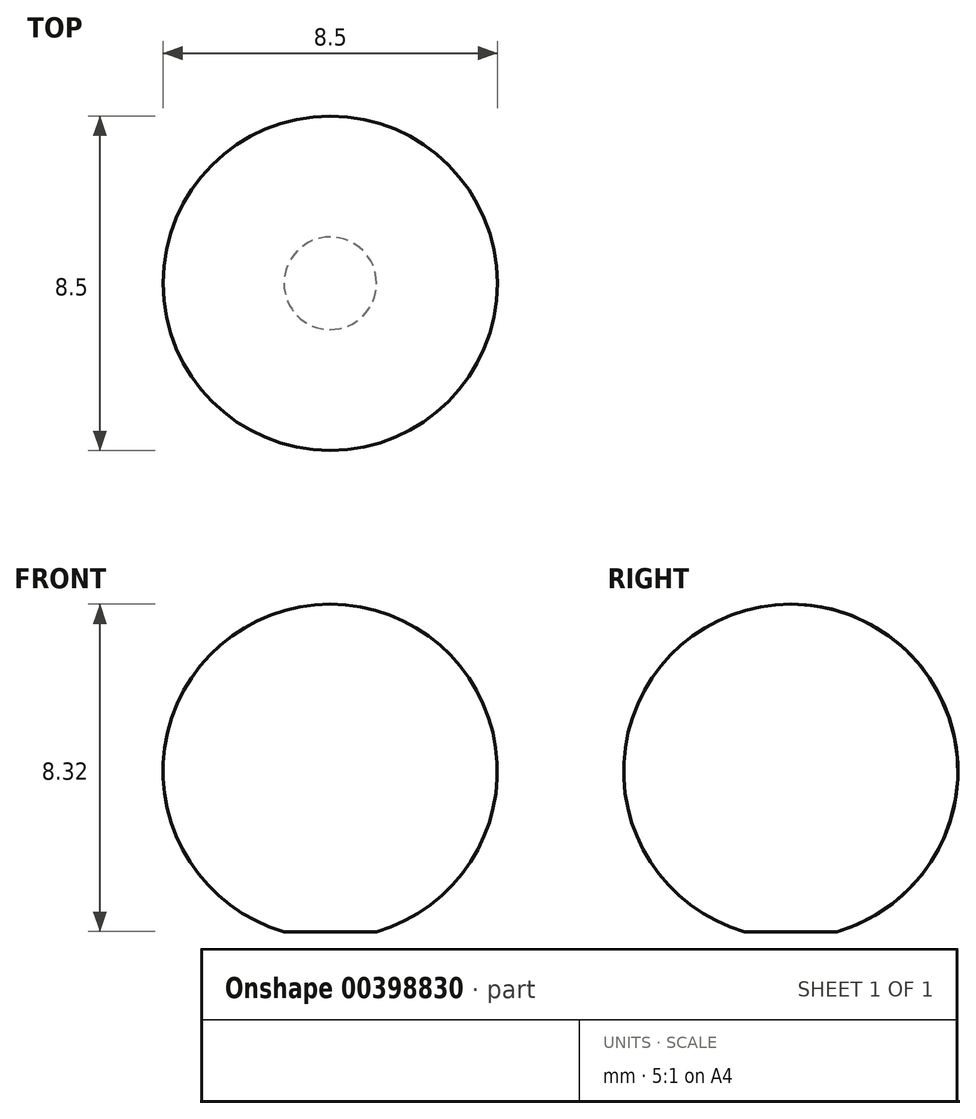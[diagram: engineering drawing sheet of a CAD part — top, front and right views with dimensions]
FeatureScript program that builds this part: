
annotation { "Feature Type Name" : "Feature", "Feature Type Description" : "" }
export const myFeature = defineFeature(function(context is Context, id is Id, definition is map)
    precondition{}
    {
        {
            var Q0;
            Q0=qCreatedBy(makeId("Right.planeOp"),FACE);
            var sketch = newSketch(context, id + "F0", { "sketchPlane" : qUnion([Q0])});
            skLineSegment(sketch, "E0", {"start": v(0, 69.75) * mm, "end": v(0, -48.06) * mm});
            skArc(sketch, "E1", {"start": v(1.18, 14.79) * mm, "mid": v(4.2, 19.46) * mm, "end": v(0, 23.11) * mm});
            skLineSegment(sketch, "E2", {"start": v(0, 14.79) * mm, "end": v(1.18, 14.79) * mm});
            skSolve(sketch);
        }
        {
            var Q0;
            {var subQ0=sQuery(id+"F0.wireOp",EDGE,"E1");Q0=makeQuery(id+"F0.imprint","IMPRINT",FACE,{"disambiguationData":[TD([[makeQuery(id+"F0.imprint","IMPRINT",EDGE,{"derivedFrom":subQ0}),1.0]])]});}
            var Q1;
            Q1=sQuery(id+"F0.wireOp",EDGE,"E0");
            revolve(context, id + "F1", {"entities" : qUnion([Q0]), "axis" : qUnion([Q1]), "revolveType" : RevolveType.FULL});
        }
    });
